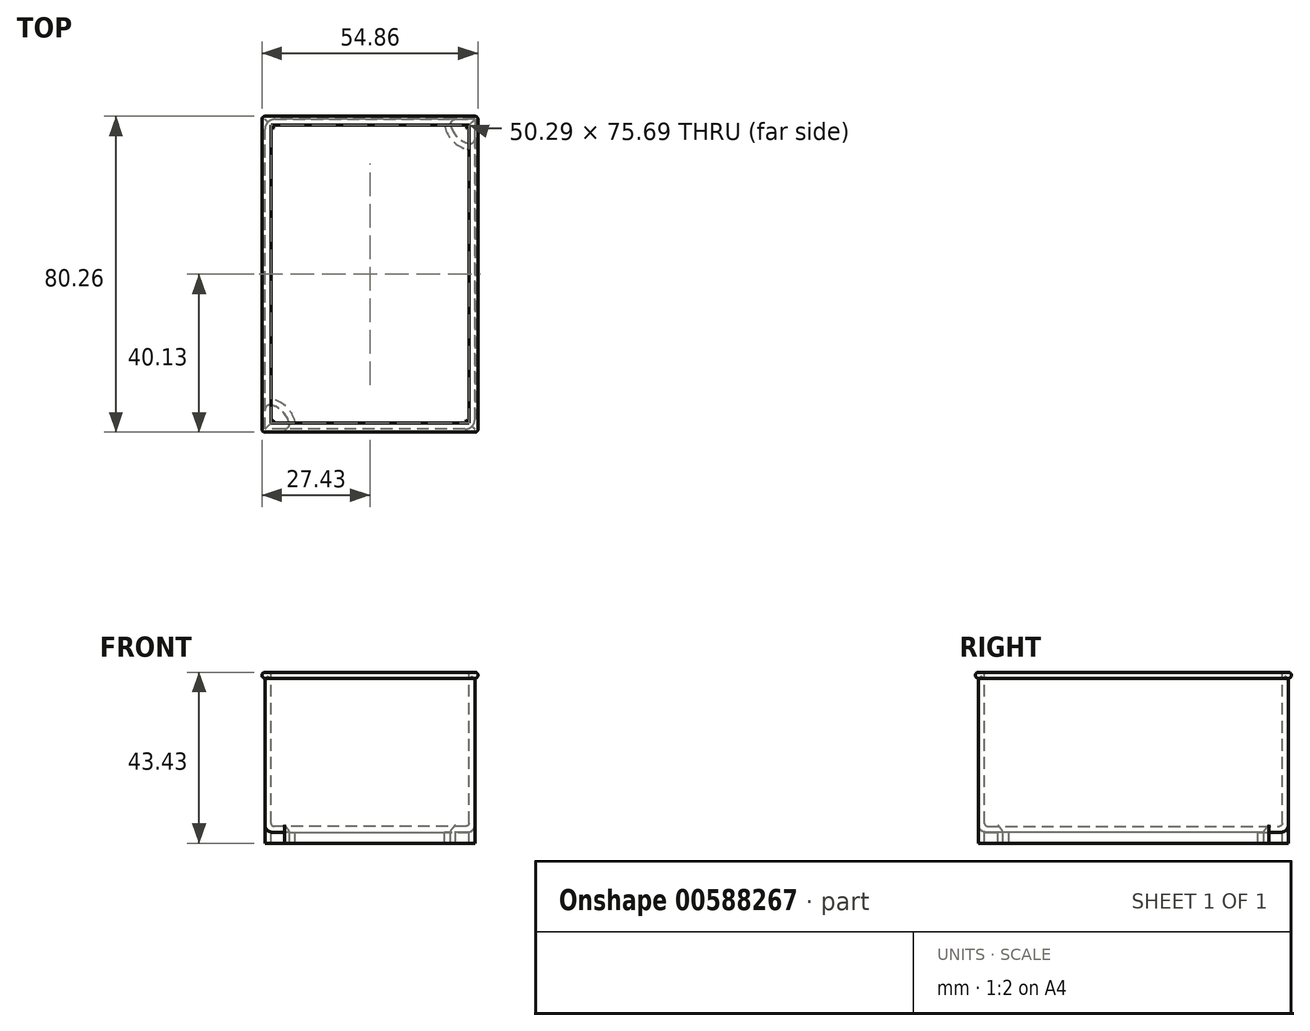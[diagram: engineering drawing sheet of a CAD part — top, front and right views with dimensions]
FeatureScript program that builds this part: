
annotation { "Feature Type Name" : "Feature", "Feature Type Description" : "" }
export const myFeature = defineFeature(function(context is Context, id is Id, definition is map)
    precondition{}
    {
        {
            var Q0;
            Q0=qCreatedBy(makeId("Front.planeOp"),FACE);
            var sketch = newSketch(context, id + "F0", { "sketchPlane" : qUnion([Q0])});
            skLineSegment(sketch, "E0.bottom", {"start": v(26.67, -20.32) * mm, "end": v(-26.67, -20.32) * mm});
            skLineSegment(sketch, "E0.top", {"start": v(26.67, 20.32) * mm, "end": v(-26.67, 20.32) * mm});
            skLineSegment(sketch, "E0.left", {"start": v(26.67, -20.32) * mm, "end": v(26.67, 20.32) * mm});
            skLineSegment(sketch, "E0.right", {"start": v(-26.67, -20.32) * mm, "end": v(-26.67, 20.32) * mm});
            skPoint(sketch, "E0.middle", {"position": v(0, 0) * mm});
            skSolve(sketch);
        }
        {
            var Q0;
            Q0=makeQuery(id+"F0.imprint","IMPRINT",FACE,{"disambiguationData":[TD([[makeQuery(id+"F0.imprint","IMPRINT",EDGE,{"derivedFrom":sQuery(id+"F0.wireOp",EDGE,"E0.bottom")}),-1.0]])]});
            extrude(context, id + "F1", {"entities" : qUnion([Q0]), "endBound" : BoundingType.SYMMETRIC, "depth" : 78.74 * mm});
        }
        {
            var Q0;
            Q0=makeQuery(id+"F1.opExtrude","SWEPT_FACE",FACE,{"disambiguationData":[OSD([sQuery(id+"F0.wireOp",EDGE,"E0.top")])]});
            shell(context, id + "F2", {"entities" : qUnion([Q0]), "thickness" : 1.52 * mm});
        }
        {
            var Q0;
            Q0=makeQuery(id+"F1.opExtrude","CAP_FACE",FACE,{"disambiguationData":[OSD([sQuery(id+"F0.wireOp",EDGE,"E0.bottom"),sQuery(id+"F0.wireOp",EDGE,"E0.top"),sQuery(id+"F0.wireOp",EDGE,"E0.left"),sQuery(id+"F0.wireOp",EDGE,"E0.right")])],"isStart":false});
            var sketch = newSketch(context, id + "F3", { "sketchPlane" : qUnion([Q0])});
            skArc(sketch, "E1", {"start": v(-26.67, 20.32) * mm, "mid": v(-27.43, 19.56) * mm, "end": v(-26.67, 18.8) * mm});
            skSolve(sketch);
        }
        {
            var Q0;
            {var subQ0=sQuery(id+"F3.wireOp",EDGE,"E1");Q0=makeQuery(id+"F3.imprint","IMPRINT",FACE,{"disambiguationData":[TD([[makeQuery(id+"F3.imprint","IMPRINT",EDGE,{"derivedFrom":subQ0}),1.0]])]});}
            var Q1;
            Q1=makeQuery(id+"F1.opExtrude","SWEPT_EDGE",EDGE,{"disambiguationData":[OSD([sQuery(id+"F0.wireOp",EDGE,"E0.top"),sQuery(id+"F0.wireOp",EDGE,"E0.right")])]});
            var Q2;
            Q2=makeQuery(id+"F1.opExtrude","CAP_EDGE",EDGE,{"disambiguationData":[OSD([sQuery(id+"F0.wireOp",EDGE,"E0.top")])],"isStart":true});
            var Q3;
            Q3=makeQuery(id+"F1.opExtrude","SWEPT_EDGE",EDGE,{"disambiguationData":[OSD([sQuery(id+"F0.wireOp",EDGE,"E0.top"),sQuery(id+"F0.wireOp",EDGE,"E0.left")])]});
            var Q4;
            Q4=makeQuery(id+"F1.opExtrude","CAP_EDGE",EDGE,{"disambiguationData":[OSD([sQuery(id+"F0.wireOp",EDGE,"E0.top")])],"isStart":false});
            sweep(context, id + "F4", {"operationType" : NewBodyOperationType.ADD, "profiles" : qUnion([Q0]), "path" : qUnion([Q1, Q2, Q3, Q4])});
        }
        {
            var Q0;
            Q0=makeQuery(id+"F1.opExtrude","SWEPT_FACE",FACE,{"disambiguationData":[OSD([sQuery(id+"F0.wireOp",EDGE,"E0.bottom")])]});
            var sketch = newSketch(context, id + "F5", { "sketchPlane" : qUnion([Q0])});
            skLineSegment(sketch, "E2.bottom", {"start": v(26.67, 39.37) * mm, "end": v(21.75, 39.37) * mm});
            skLineSegment(sketch, "E2.left", {"start": v(26.67, 39.37) * mm, "end": v(26.67, 34.45) * mm});
            skPoint(sketch, "E3.newPointA", {"position": v(20.32, 19.05) * mm});
            skArc(sketch, "E4", {"start": v(20.52, 37.78) * mm, "mid": v(22.18, 34.88) * mm, "end": v(25.08, 33.22) * mm});
            skPoint(sketch, "E5.visualSharp", {"position": v(20.32, 39.37) * mm});
            skArc(sketch, "E5.filletArc", {"start": v(21.75, 39.37) * mm, "mid": v(20.75, 38.88) * mm, "end": v(20.52, 37.78) * mm});
            skPoint(sketch, "E6.visualSharp", {"position": v(26.67, 33.02) * mm});
            skArc(sketch, "E6.filletArc", {"start": v(25.08, 33.22) * mm, "mid": v(26.18, 33.45) * mm, "end": v(26.67, 34.45) * mm});
            skArc(sketch, "E7.MirrorCS", {"start": v(-21.75, 39.37) * mm, "mid": v(-20.75, 38.88) * mm, "end": v(-20.52, 37.78) * mm});
            skArc(sketch, "E8.MirrorCS", {"start": v(-20.52, 37.78) * mm, "mid": v(-22.18, 34.88) * mm, "end": v(-25.08, 33.22) * mm});
            skArc(sketch, "E9.MirrorCS", {"start": v(-25.08, 33.22) * mm, "mid": v(-26.18, 33.45) * mm, "end": v(-26.67, 34.45) * mm});
            skLineSegment(sketch, "E10.MirrorCS", {"start": v(-26.67, 39.37) * mm, "end": v(-26.67, 34.45) * mm});
            skLineSegment(sketch, "E11.MirrorCS", {"start": v(-26.67, 39.37) * mm, "end": v(-21.75, 39.37) * mm});
            skArc(sketch, "E12.MirrorCS", {"start": v(-20.52, -37.78) * mm, "mid": v(-22.18, -34.88) * mm, "end": v(-25.08, -33.22) * mm});
            skArc(sketch, "E13.MirrorCS", {"start": v(-21.75, -39.37) * mm, "mid": v(-20.75, -38.88) * mm, "end": v(-20.52, -37.78) * mm});
            skLineSegment(sketch, "E14.MirrorCS", {"start": v(-26.67, -39.37) * mm, "end": v(-21.75, -39.37) * mm});
            skLineSegment(sketch, "E15.MirrorCS", {"start": v(-26.67, -39.37) * mm, "end": v(-26.67, -34.45) * mm});
            skArc(sketch, "E16.MirrorCS", {"start": v(-25.08, -33.22) * mm, "mid": v(-26.18, -33.45) * mm, "end": v(-26.67, -34.45) * mm});
            skArc(sketch, "E17.MirrorCS", {"start": v(21.75, -39.37) * mm, "mid": v(20.75, -38.88) * mm, "end": v(20.52, -37.78) * mm});
            skArc(sketch, "E18.MirrorCS", {"start": v(20.52, -37.78) * mm, "mid": v(22.18, -34.88) * mm, "end": v(25.08, -33.22) * mm});
            skArc(sketch, "E19.MirrorCS", {"start": v(25.08, -33.22) * mm, "mid": v(26.18, -33.45) * mm, "end": v(26.67, -34.45) * mm});
            skLineSegment(sketch, "E20.MirrorCS", {"start": v(26.67, -39.37) * mm, "end": v(26.67, -34.45) * mm});
            skLineSegment(sketch, "E21.MirrorCS", {"start": v(26.67, -39.37) * mm, "end": v(21.75, -39.37) * mm});
            skSolve(sketch);
        }
        {
            var Q0;
            Q0=makeQuery(id+"F5.imprint","IMPRINT",FACE,{"disambiguationData":[TD([[makeQuery(id+"F5.imprint","IMPRINT",EDGE,{"derivedFrom":sQuery(id+"F5.wireOp",EDGE,"E2.bottom")}),1.0]])]});
            var Q1;
            Q1=makeQuery(id+"F5.imprint","IMPRINT",FACE,{"disambiguationData":[TD([[makeQuery(id+"F5.imprint","IMPRINT",EDGE,{"derivedFrom":sQuery(id+"F5.wireOp",EDGE,"E8.MirrorCS")}),-1.0]])]});
            var Q2;
            Q2=makeQuery(id+"F5.imprint","IMPRINT",FACE,{"disambiguationData":[TD([[makeQuery(id+"F5.imprint","IMPRINT",EDGE,{"derivedFrom":sQuery(id+"F5.wireOp",EDGE,"E12.MirrorCS")}),1.0]])]});
            var Q3;
            Q3=makeQuery(id+"F5.imprint","IMPRINT",FACE,{"disambiguationData":[TD([[makeQuery(id+"F5.imprint","IMPRINT",EDGE,{"derivedFrom":sQuery(id+"F5.wireOp",EDGE,"E17.MirrorCS")}),-1.0]])]});
            extrude(context, id + "F6", {"entities" : qUnion([Q0, Q1, Q2, Q3]), "operationType" : NewBodyOperationType.ADD, "depth" : 2.8 * mm});
        }
        {
            var Q0;
            Q0=makeQuery(id+"F6.opExtrude","CAP_FACE",FACE,{"disambiguationData":[OSD([sQuery(id+"F5.wireOp",EDGE,"E2.bottom"),sQuery(id+"F5.wireOp",EDGE,"E2.left"),sQuery(id+"F5.wireOp",EDGE,"E4"),sQuery(id+"F5.wireOp",EDGE,"E5.filletArc"),sQuery(id+"F5.wireOp",EDGE,"E6.filletArc")])],"isStart":false});
            var Q1;
            Q1=makeQuery(id+"F6.opExtrude","CAP_FACE",FACE,{"disambiguationData":[OSD([sQuery(id+"F5.wireOp",EDGE,"E8.MirrorCS"),sQuery(id+"F5.wireOp",EDGE,"E9.MirrorCS"),sQuery(id+"F5.wireOp",EDGE,"E10.MirrorCS"),sQuery(id+"F5.wireOp",EDGE,"E7.MirrorCS"),sQuery(id+"F5.wireOp",EDGE,"E11.MirrorCS")])],"isStart":false});
            var Q2;
            Q2=makeQuery(id+"F6.opExtrude","CAP_FACE",FACE,{"disambiguationData":[OSD([sQuery(id+"F5.wireOp",EDGE,"E12.MirrorCS"),sQuery(id+"F5.wireOp",EDGE,"E13.MirrorCS"),sQuery(id+"F5.wireOp",EDGE,"E14.MirrorCS"),sQuery(id+"F5.wireOp",EDGE,"E15.MirrorCS"),sQuery(id+"F5.wireOp",EDGE,"E16.MirrorCS")])],"isStart":false});
            var Q3;
            Q3=makeQuery(id+"F6.opExtrude","CAP_FACE",FACE,{"disambiguationData":[OSD([sQuery(id+"F5.wireOp",EDGE,"E17.MirrorCS"),sQuery(id+"F5.wireOp",EDGE,"E18.MirrorCS"),sQuery(id+"F5.wireOp",EDGE,"E19.MirrorCS"),sQuery(id+"F5.wireOp",EDGE,"E20.MirrorCS"),sQuery(id+"F5.wireOp",EDGE,"E21.MirrorCS")])],"isStart":false});
            shell(context, id + "F7", {"entities" : qUnion([Q0, Q1, Q2, Q3]), "thickness" : 1.52 * mm});
        }
        {
            var Q0;
            Q0=makeQuery(id+"F2.opShell","OFFSET_FACE",FACE,{"disambiguationData":[OSD([sQuery(id+"F0.wireOp",EDGE,"E0.bottom")])]});
            fillet(context, id + "F8", {"entities" : qUnion([Q0]), "radius" : 0.76 * mm, "tangentPropagation" : true, "allowEdgeOverflow" : false});
        }
        {
            var Q0;
            Q0=makeQuery(id+"F1.opExtrude","SWEPT_EDGE",EDGE,{"disambiguationData":[OSD([sQuery(id+"F0.wireOp",EDGE,"E0.bottom"),sQuery(id+"F0.wireOp",EDGE,"E0.right")])]});
            var Q1;
            Q1=makeQuery(id+"F1.opExtrude","CAP_EDGE",EDGE,{"disambiguationData":[OSD([sQuery(id+"F0.wireOp",EDGE,"E0.bottom")])],"isStart":false});
            var Q2;
            Q2=makeQuery(id+"F1.opExtrude","SWEPT_EDGE",EDGE,{"disambiguationData":[OSD([sQuery(id+"F0.wireOp",EDGE,"E0.bottom"),sQuery(id+"F0.wireOp",EDGE,"E0.left")])]});
            var Q3;
            Q3=makeQuery(id+"F1.opExtrude","CAP_EDGE",EDGE,{"disambiguationData":[OSD([sQuery(id+"F0.wireOp",EDGE,"E0.bottom")])],"isStart":true});
            fillet(context, id + "F9", {"entities" : qUnion([Q0, Q1, Q2, Q3]), "radius" : 1.9 * mm, "tangentPropagation" : true, "allowEdgeOverflow" : false});
        }
        {
            var Q0;
            Q0=makeQuery(id+"F4.opSweep","MID_CAP_EDGE",EDGE,{"disambiguationData":[OSD([sQuery(id+"F0.wireOp",EDGE,"E0.top"),sQuery(id+"F0.wireOp",EDGE,"E0.left"),sQuery(id+"F3.wireOp",EDGE,"E1")])],"capPos":3.0});
            var Q1;
            Q1=makeQuery(id+"F4.opSweep","MID_CAP_EDGE",EDGE,{"disambiguationData":[OSD([sQuery(id+"F0.wireOp",EDGE,"E0.top"),sQuery(id+"F0.wireOp",EDGE,"E0.left"),sQuery(id+"F3.wireOp",EDGE,"E1")])],"capPos":2.0});
            var Q2;
            Q2=makeQuery(id+"F4.opSweep","MID_CAP_EDGE",EDGE,{"disambiguationData":[OSD([sQuery(id+"F0.wireOp",EDGE,"E0.top"),sQuery(id+"F0.wireOp",EDGE,"E0.right"),sQuery(id+"F3.wireOp",EDGE,"E1")])],"capPos":1.0});
            var Q3;
            Q3=makeQuery(id+"F4.opSweep","CAP_EDGE",EDGE,{"disambiguationData":[OSD([sQuery(id+"F0.wireOp",EDGE,"E0.top"),sQuery(id+"F0.wireOp",EDGE,"E0.right"),sQuery(id+"F3.wireOp",EDGE,"E1")])],"isStart":true});
            fillet(context, id + "F10", {"entities" : qUnion([Q0, Q1, Q2, Q3]), "radius" : 0.76 * mm, "tangentPropagation" : true, "allowEdgeOverflow" : false});
        }
        {
            var Q0;
            Q0=makeQuery(id+"F6.boolean.opBoolean","MERGE",EDGE,{"derivedFrom":[makeQuery(id+"F1.opExtrude","CAP_EDGE",EDGE,{"disambiguationData":[OSD([sQuery(id+"F0.wireOp",EDGE,"E0.left")])],"isStart":false}),makeQuery(id+"F6.opExtrude","SWEPT_EDGE",EDGE,{"disambiguationData":[OSD([sQuery(id+"F5.wireOp",EDGE,"E2.bottom"),sQuery(id+"F5.wireOp",EDGE,"E2.left")])]})]});
            var Q1;
            Q1=makeQuery(id+"F6.boolean.opBoolean","MERGE",EDGE,{"derivedFrom":[makeQuery(id+"F1.opExtrude","CAP_EDGE",EDGE,{"disambiguationData":[OSD([sQuery(id+"F0.wireOp",EDGE,"E0.left")])],"isStart":true}),makeQuery(id+"F6.opExtrude","SWEPT_EDGE",EDGE,{"disambiguationData":[OSD([sQuery(id+"F5.wireOp",EDGE,"E20.MirrorCS"),sQuery(id+"F5.wireOp",EDGE,"E21.MirrorCS")])]})]});
            var Q2;
            Q2=makeQuery(id+"F6.boolean.opBoolean","MERGE",EDGE,{"derivedFrom":[makeQuery(id+"F1.opExtrude","CAP_EDGE",EDGE,{"disambiguationData":[OSD([sQuery(id+"F0.wireOp",EDGE,"E0.right")])],"isStart":false}),makeQuery(id+"F6.opExtrude","SWEPT_EDGE",EDGE,{"disambiguationData":[OSD([sQuery(id+"F5.wireOp",EDGE,"E10.MirrorCS"),sQuery(id+"F5.wireOp",EDGE,"E11.MirrorCS")])]})]});
            var Q3;
            Q3=makeQuery(id+"F6.boolean.opBoolean","MERGE",EDGE,{"derivedFrom":[makeQuery(id+"F1.opExtrude","CAP_EDGE",EDGE,{"disambiguationData":[OSD([sQuery(id+"F0.wireOp",EDGE,"E0.right")])],"isStart":true}),makeQuery(id+"F6.opExtrude","SWEPT_EDGE",EDGE,{"disambiguationData":[OSD([sQuery(id+"F5.wireOp",EDGE,"E14.MirrorCS"),sQuery(id+"F5.wireOp",EDGE,"E15.MirrorCS")])]})]});
            fillet(context, id + "F11", {"entities" : qUnion([Q0, Q1, Q2, Q3]), "radius" : 2.54 * mm, "tangentPropagation" : true, "allowEdgeOverflow" : false});
        }
        {
            var Q0;
            Q0=makeQuery(id+"F1.opExtrude","SWEPT_BODY",BODY,{"disambiguationData":[OSD([sQuery(id+"F0.wireOp",EDGE,"E0.bottom"),sQuery(id+"F0.wireOp",EDGE,"E0.top"),sQuery(id+"F0.wireOp",EDGE,"E0.left"),sQuery(id+"F0.wireOp",EDGE,"E0.right")])]});
            transform(context, id + "F12", {"entities" : qUnion([Q0]), "transformType" : TransformType.COPY});
        }
        {
            var Q0;
            Q0=makeQuery(id+"F12.opPattern","COPY",BODY,{"derivedFrom":makeQuery(id+"F1.opExtrude","SWEPT_BODY",BODY,{"disambiguationData":[OSD([sQuery(id+"F0.wireOp",EDGE,"E0.bottom"),sQuery(id+"F0.wireOp",EDGE,"E0.top"),sQuery(id+"F0.wireOp",EDGE,"E0.left"),sQuery(id+"F0.wireOp",EDGE,"E0.right")])]}),"instanceName":"1"});
            deleteBodies(context, id + "F13", {"entities" : qUnion([Q0])});
        }
    });
